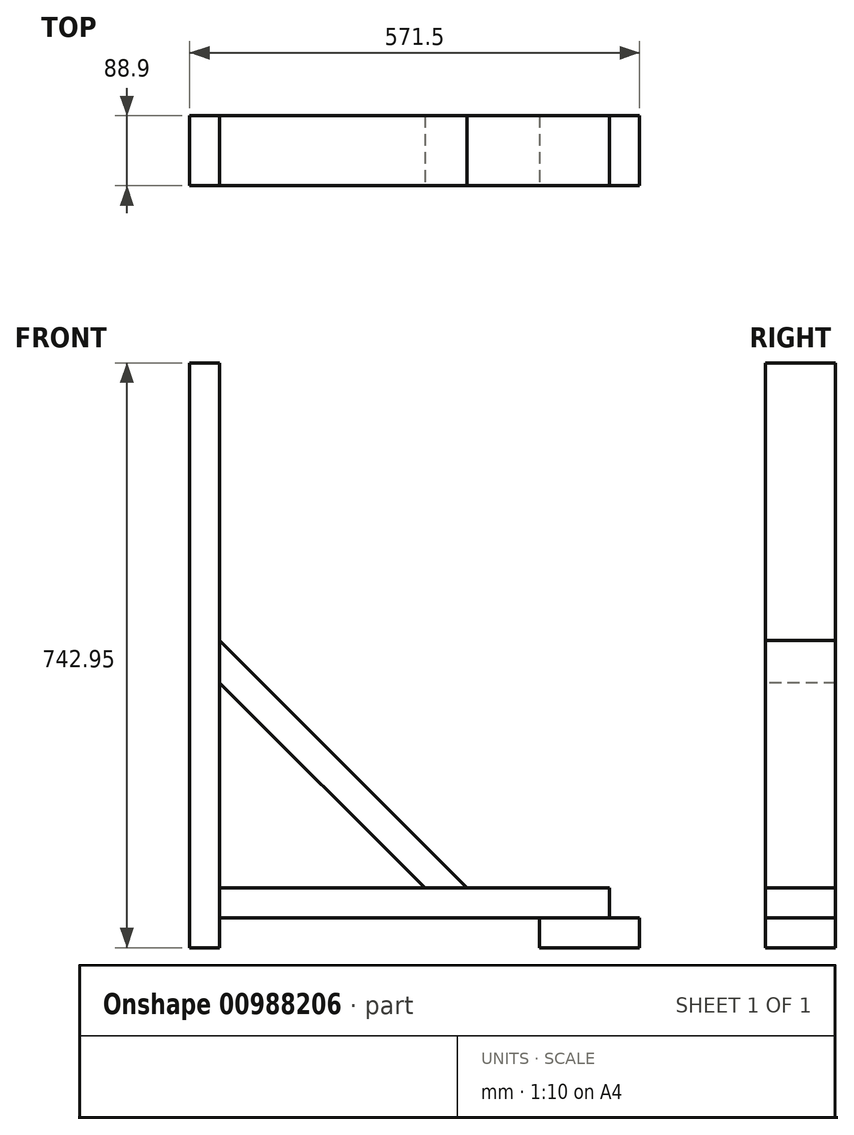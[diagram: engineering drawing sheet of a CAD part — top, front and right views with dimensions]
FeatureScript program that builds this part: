
annotation { "Feature Type Name" : "Feature", "Feature Type Description" : "" }
export const myFeature = defineFeature(function(context is Context, id is Id, definition is map)
    precondition{}
    {
        {
            var Q0;
            Q0=qCreatedBy(makeId("Top.planeOp"),FACE);
            var sketch = newSketch(context, id + "F0", { "sketchPlane" : qUnion([Q0])});
            skLineSegment(sketch, "E0.bottom", {"start": v(19.05, -44.45) * mm, "end": v(-19.05, -44.45) * mm});
            skLineSegment(sketch, "E0.top", {"start": v(19.05, 44.45) * mm, "end": v(-19.05, 44.45) * mm});
            skLineSegment(sketch, "E0.left", {"start": v(19.05, -44.45) * mm, "end": v(19.05, 44.45) * mm});
            skLineSegment(sketch, "E0.right", {"start": v(-19.05, -44.45) * mm, "end": v(-19.05, 44.45) * mm});
            skPoint(sketch, "E0.middle", {"position": v(0, 0) * mm});
            skSolve(sketch);
        }
        {
            var Q0;
            Q0=makeQuery(id+"F0.imprint","IMPRINT",FACE,{"disambiguationData":[TD([[makeQuery(id+"F0.imprint","IMPRINT",EDGE,{"derivedFrom":sQuery(id+"F0.wireOp",EDGE,"E0.bottom")}),-1.0]])]});
            extrude(context, id + "F1", {"entities" : qUnion([Q0]), "depth" : 742.95 * mm, "offsetDistance" : 25.4 * mm});
        }
        {
            var Q0;
            Q0=makeQuery(id+"F1.opExtrude","SWEPT_FACE",FACE,{"disambiguationData":[OSD([sQuery(id+"F0.wireOp",EDGE,"E0.bottom")])]});
            var sketch = newSketch(context, id + "F2", { "sketchPlane" : qUnion([Q0])});
            skLineSegment(sketch, "E1", {"start": v(19.05, 336.63) * mm, "end": v(279.48, 76.2) * mm});
            skLineSegment(sketch, "E2", {"start": v(333.36, 76.2) * mm, "end": v(19.05, 390.5) * mm});
            skLineSegment(sketch, "E3", {"start": v(19.05, 336.63) * mm, "end": v(5.58, 350.1) * mm, "construction": true});
            skLineSegment(sketch, "E4", {"start": v(5.58, 350.1) * mm, "end": v(19.05, 363.57) * mm, "construction": true});
            skLineSegment(sketch, "E5", {"start": v(19.05, 363.57) * mm, "end": v(19.05, 390.5) * mm});
            skLineSegment(sketch, "E6", {"start": v(19.05, 336.63) * mm, "end": v(19.05, 363.57) * mm});
            skLineSegment(sketch, "E7", {"start": v(279.48, 76.2) * mm, "end": v(333.36, 76.2) * mm});
            skLineSegment(sketch, "E8", {"start": v(19.05, 336.63) * mm, "end": v(19.05, 76.2) * mm, "construction": true});
            skLineSegment(sketch, "E9", {"start": v(19.05, 76.2) * mm, "end": v(279.48, 76.2) * mm});
            skLineSegment(sketch, "E10", {"start": v(59.46, 350.1) * mm, "end": v(-4.04, 350.1) * mm, "construction": true});
            skLineSegment(sketch, "E11", {"start": v(19.05, 38.1) * mm, "end": v(514.35, 38.1) * mm});
            skLineSegment(sketch, "E12", {"start": v(514.35, 38.1) * mm, "end": v(514.35, 76.2) * mm});
            skLineSegment(sketch, "E13", {"start": v(514.35, 76.2) * mm, "end": v(333.36, 76.2) * mm});
            skLineSegment(sketch, "E14", {"start": v(19.05, 742.95) * mm, "end": v(514.35, 742.95) * mm, "construction": true});
            skLineSegment(sketch, "E15", {"start": v(514.35, 742.95) * mm, "end": v(514.35, 704.85) * mm, "construction": true});
            skLineSegment(sketch, "E16", {"start": v(514.35, 704.85) * mm, "end": v(19.05, 704.85) * mm, "construction": true});
            skLineSegment(sketch, "E17", {"start": v(514.35, 76.2) * mm, "end": v(514.35, 704.85) * mm, "construction": true});
            skLineSegment(sketch, "E18", {"start": v(514.35, 390.53) * mm, "end": v(19.05, 390.53) * mm, "construction": true});
            skLineSegment(sketch, "E19", {"start": v(425.45, 38.1) * mm, "end": v(425.45, 0) * mm});
            skLineSegment(sketch, "E20", {"start": v(425.45, 0) * mm, "end": v(552.45, 0) * mm});
            skLineSegment(sketch, "E21", {"start": v(552.45, 0) * mm, "end": v(552.45, 38.1) * mm});
            skLineSegment(sketch, "E22", {"start": v(552.45, 38.1) * mm, "end": v(514.35, 38.1) * mm});
            skSolve(sketch);
        }
        {
            var Q0;
            Q0=makeQuery(id+"F2.imprint","IMPRINT",FACE,{"disambiguationData":[TD([[makeQuery(id+"F2.imprint","IMPRINT",EDGE,{"derivedFrom":sQuery(id+"F2.wireOp",EDGE,"E7")}),-1.0]])]});
            extrude(context, id + "F3", {"entities" : qUnion([Q0]), "oppositeDirection" : true, "depth" : 88.9 * mm, "offsetDistance" : 25.4 * mm});
        }
        {
            var Q0;
            Q0=makeQuery(id+"F2.imprint","IMPRINT",FACE,{"disambiguationData":[TD([[makeQuery(id+"F2.imprint","IMPRINT",EDGE,{"derivedFrom":sQuery(id+"F2.wireOp",EDGE,"E1")}),1.0]])]});
            extrude(context, id + "F4", {"entities" : qUnion([Q0]), "oppositeDirection" : true, "depth" : 88.9 * mm, "offsetDistance" : 25.4 * mm});
        }
        {
            var Q0;
            {var subQ0=sQuery(id+"F2.wireOp",EDGE,"E19");Q0=makeQuery(id+"F2.imprint","IMPRINT",FACE,{"disambiguationData":[TD([[makeQuery(id+"F2.imprint","IMPRINT",EDGE,{"derivedFrom":subQ0}),1.0]])]});}
            extrude(context, id + "F5", {"entities" : qUnion([Q0]), "oppositeDirection" : true, "depth" : 88.9 * mm, "offsetDistance" : 25.4 * mm});
        }
    });
